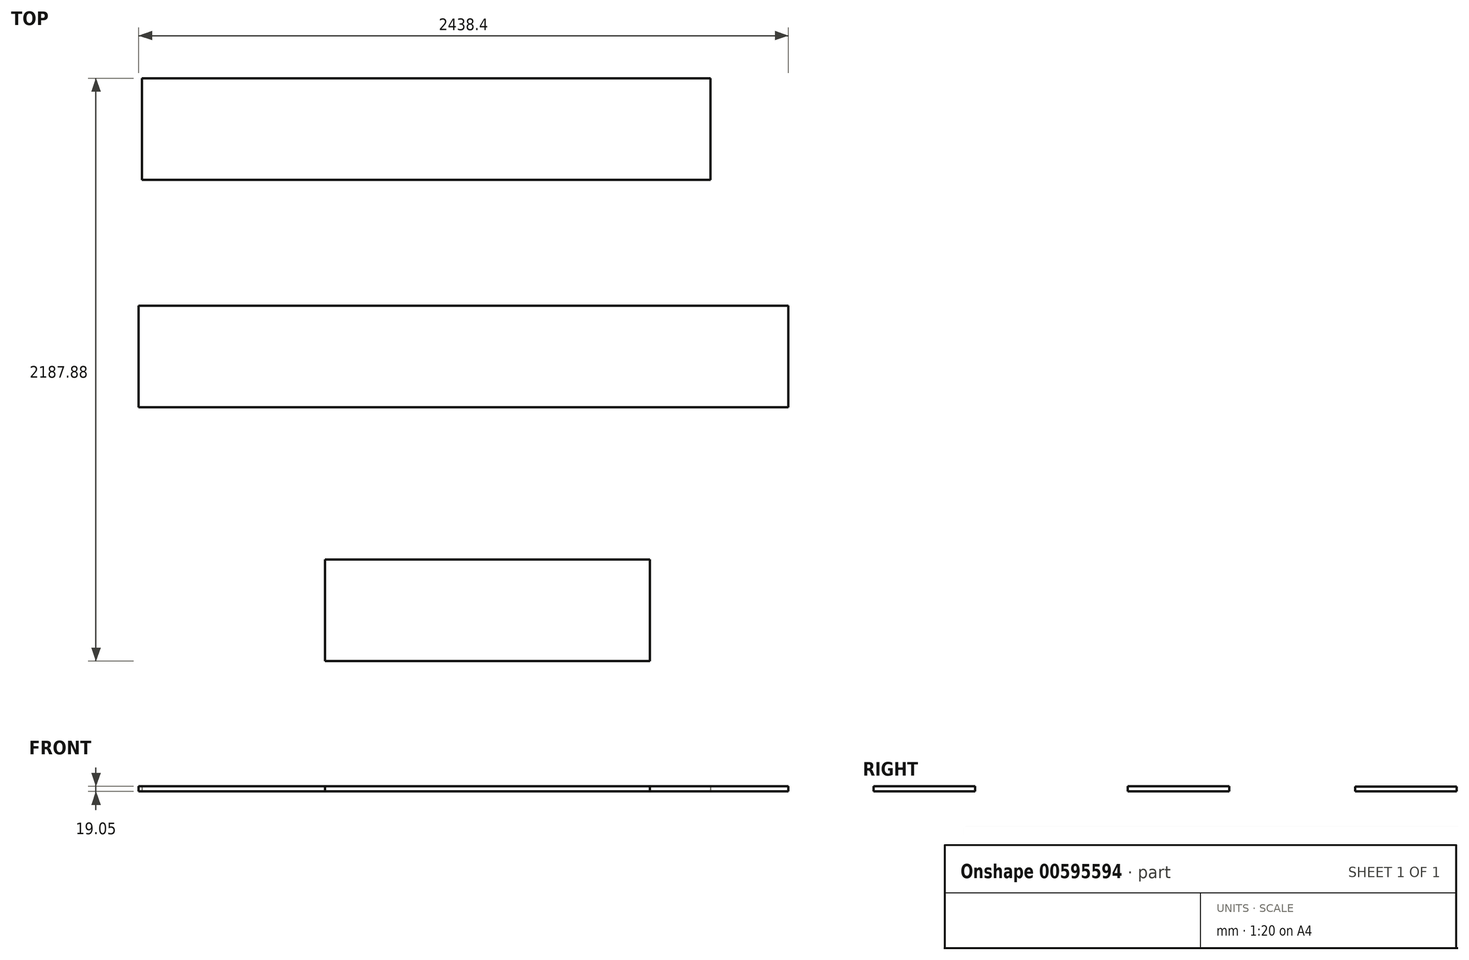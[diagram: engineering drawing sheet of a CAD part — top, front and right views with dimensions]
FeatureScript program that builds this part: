
annotation { "Feature Type Name" : "Feature", "Feature Type Description" : "" }
export const myFeature = defineFeature(function(context is Context, id is Id, definition is map)
    precondition{}
    {
        {
            var Q0;
            Q0=qCreatedBy(makeId("Top.planeOp"),FACE);
            var sketch = newSketch(context, id + "F0", { "sketchPlane" : qUnion([Q0])});
            skLineSegment(sketch, "E0.bottom", {"start": v(-609.6, 190.5) * mm, "end": v(609.6, 190.5) * mm});
            skLineSegment(sketch, "E0.top", {"start": v(-609.6, -190.5) * mm, "end": v(609.6, -190.5) * mm});
            skLineSegment(sketch, "E0.left", {"start": v(-609.6, 190.5) * mm, "end": v(-609.6, -190.5) * mm});
            skLineSegment(sketch, "E0.right", {"start": v(609.6, 190.5) * mm, "end": v(609.6, -190.5) * mm});
            skPoint(sketch, "E0.middle", {"position": v(0, 0) * mm});
            skSolve(sketch);
        }
        {
            var Q0;
            Q0 = qSketchRegion(id + "F0", true);
            extrude(context, id + "F1", {"entities" : qUnion([Q0]), "depth" : 19.05 * mm, "offsetDistance" : 25.4 * mm});
        }
        {
            var Q0;
            Q0=qCreatedBy(makeId("Top.planeOp"),FACE);
            var sketch = newSketch(context, id + "F2", { "sketchPlane" : qUnion([Q0])});
            skLineSegment(sketch, "E1.bottom", {"start": v(1129.64, 1143.66) * mm, "end": v(-1308.76, 1143.66) * mm});
            skLineSegment(sketch, "E1.top", {"start": v(1129.64, 762.66) * mm, "end": v(-1308.76, 762.66) * mm});
            skLineSegment(sketch, "E1.left", {"start": v(1129.64, 1143.66) * mm, "end": v(1129.64, 762.66) * mm});
            skLineSegment(sketch, "E1.right", {"start": v(-1308.76, 1143.66) * mm, "end": v(-1308.76, 762.66) * mm});
            skPoint(sketch, "E1.middle", {"position": v(-89.56, 953.16) * mm});
            skSolve(sketch);
        }
        {
            var Q0;
            Q0 = qSketchRegion(id + "F2", true);
            extrude(context, id + "F3", {"entities" : qUnion([Q0]), "depth" : 19.05 * mm, "offsetDistance" : 25.4 * mm});
        }
        {
            var Q0;
            Q0=qCreatedBy(makeId("Top.planeOp"),FACE);
            var sketch = newSketch(context, id + "F4", { "sketchPlane" : qUnion([Q0])});
            skLineSegment(sketch, "E2.bottom", {"start": v(837.34, 1997.38) * mm, "end": v(-1296.26, 1997.38) * mm});
            skLineSegment(sketch, "E2.top", {"start": v(837.34, 1616.38) * mm, "end": v(-1296.26, 1616.38) * mm});
            skLineSegment(sketch, "E2.left", {"start": v(837.34, 1997.38) * mm, "end": v(837.34, 1616.38) * mm});
            skLineSegment(sketch, "E2.right", {"start": v(-1296.26, 1997.38) * mm, "end": v(-1296.26, 1616.38) * mm});
            skPoint(sketch, "E2.middle", {"position": v(-229.46, 1806.88) * mm});
            skSolve(sketch);
        }
        {
            var Q0;
            Q0 = qSketchRegion(id + "F4", true);
            extrude(context, id + "F5", {"entities" : qUnion([Q0]), "depth" : 18.8 * mm, "offsetDistance" : 25.4 * mm});
        }
        {
            var Q0;
            Q0=qCreatedBy(makeId("Top.planeOp"),FACE);
            var sketch = newSketch(context, id + "F6", { "sketchPlane" : qUnion([Q0])});
            skLineSegment(sketch, "E3.bottom", {"start": v(-804.75, -1433.92) * mm, "end": v(1633.65, -1433.92) * mm});
            skLineSegment(sketch, "E3.top", {"start": v(-804.75, -1052.92) * mm, "end": v(1633.65, -1052.92) * mm});
            skLineSegment(sketch, "E3.left", {"start": v(-804.75, -1433.92) * mm, "end": v(-804.75, -1052.92) * mm});
            skLineSegment(sketch, "E3.right", {"start": v(1633.65, -1433.92) * mm, "end": v(1633.65, -1052.92) * mm});
            skSolve(sketch);
        }
        {
            var Q0;
            Q0 = qSketchRegion(id + "F6", true);
            extrude(context, id + "F7", {"entities" : qUnion([Q0]), "depth" : 19.05 * mm, "offsetDistance" : 25.4 * mm});
        }
        {
            var Q0;
            Q0=makeQuery(id+"F7.opExtrude","SWEPT_BODY",BODY,{"disambiguationData":[OSD([sQuery(id+"F6.wireOp",EDGE,"E3.bottom"),sQuery(id+"F6.wireOp",EDGE,"E3.top"),sQuery(id+"F6.wireOp",EDGE,"E3.left"),sQuery(id+"F6.wireOp",EDGE,"E3.right")])]});
            deleteBodies(context, id + "F8", {"entities" : qUnion([Q0])});
        }
    });
